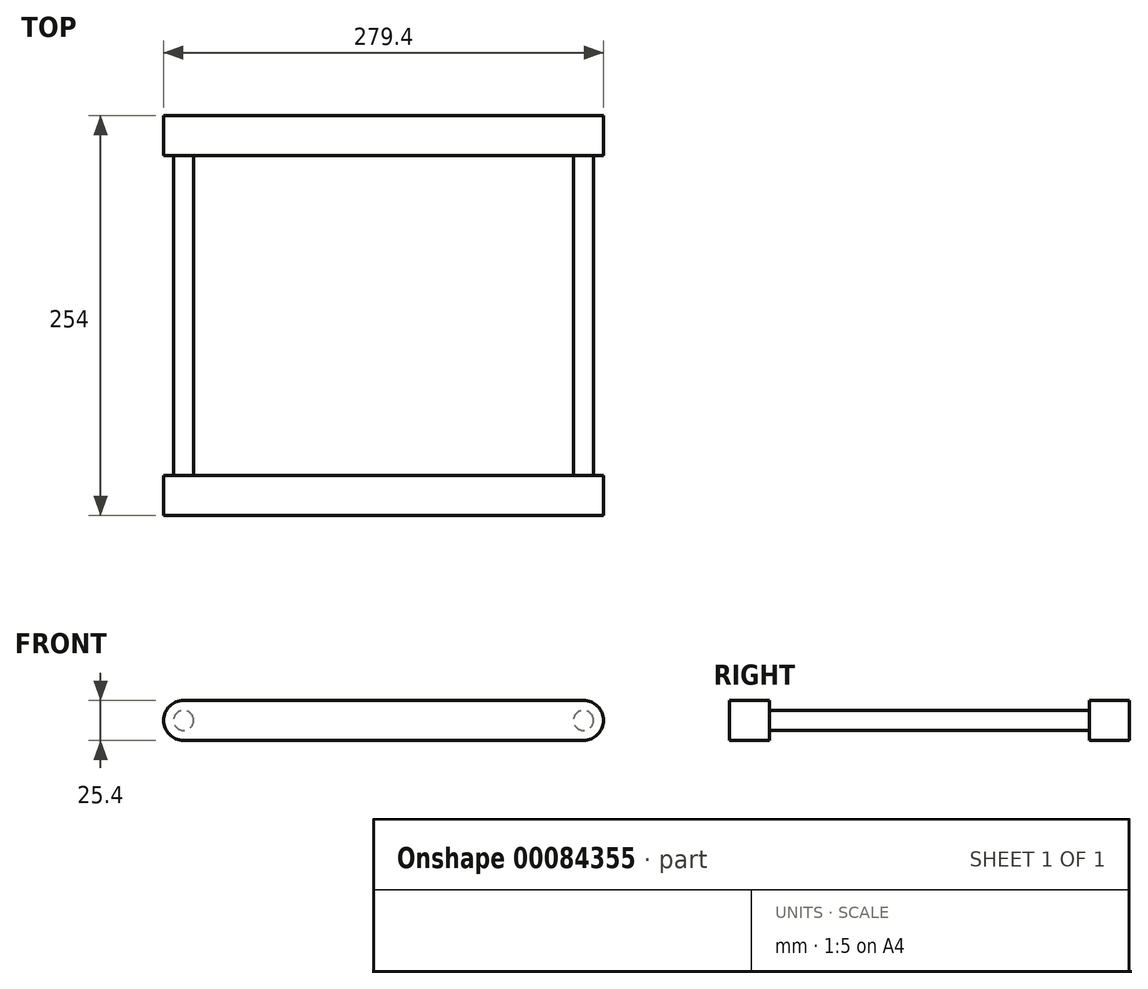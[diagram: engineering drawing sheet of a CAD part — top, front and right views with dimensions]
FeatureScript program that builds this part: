
annotation { "Feature Type Name" : "Feature", "Feature Type Description" : "" }
export const myFeature = defineFeature(function(context is Context, id is Id, definition is map)
    precondition{}
    {
        {
            var Q0;
            Q0=qCreatedBy(makeId("Front.planeOp"),FACE);
            var sketch = newSketch(context, id + "F0", { "sketchPlane" : qUnion([Q0])});
            skArc(sketch, "E0", {"start": v(0, -12.7) * mm, "mid": v(12.7, 0) * mm, "end": v(0, 12.7) * mm});
            skArc(sketch, "E1", {"start": v(-254, 12.7) * mm, "mid": v(-266.7, 0) * mm, "end": v(-254, -12.7) * mm});
            skLineSegment(sketch, "E2", {"start": v(-254, 12.7) * mm, "end": v(0, 12.7) * mm});
            skLineSegment(sketch, "E3", {"start": v(-254, -12.7) * mm, "end": v(0, -12.7) * mm});
            skLineSegment(sketch, "E4", {"start": v(0, 12.7) * mm, "end": v(-254, -12.7) * mm, "construction": true});
            skLineSegment(sketch, "E5", {"start": v(-254, 12.7) * mm, "end": v(0, -12.7) * mm, "construction": true});
            skSolve(sketch);
        }
        {
            var Q0;
            Q0=makeQuery(id+"F0.imprint","IMPRINT",FACE,{"disambiguationData":[TD([[makeQuery(id+"F0.imprint","IMPRINT",EDGE,{"derivedFrom":sQuery(id+"F0.wireOp",EDGE,"E0")}),1.0]])]});
            extrude(context, id + "F1", {"entities" : qUnion([Q0]), "depth" : 25.4 * mm});
        }
        {
            var Q0;
            Q0=makeQuery(id+"F1.opExtrude","CAP_FACE",FACE,{"disambiguationData":[OSD([sQuery(id+"F0.wireOp",EDGE,"E0"),sQuery(id+"F0.wireOp",EDGE,"E1"),sQuery(id+"F0.wireOp",EDGE,"E2"),sQuery(id+"F0.wireOp",EDGE,"E3")])],"isStart":false});
            var sketch = newSketch(context, id + "F2", { "sketchPlane" : qUnion([Q0])});
            skLineSegment(sketch, "E6.0", {"start": v(-254, 12.7) * mm, "end": v(0, 12.7) * mm});
            skArc(sketch, "E6.1", {"start": v(-254, 12.7) * mm, "mid": v(-266.7, 0) * mm, "end": v(-254, -12.7) * mm});
            skLineSegment(sketch, "E6.2", {"start": v(-254, -12.7) * mm, "end": v(0, -12.7) * mm});
            skArc(sketch, "E6.3", {"start": v(0, -12.7) * mm, "mid": v(12.7, 0) * mm, "end": v(0, 12.7) * mm});
            skCircle(sketch, "E7", {"center": v(-254, 0) * mm, "radius": 6.35 * mm});
            skCircle(sketch, "E8", {"center": v(0, 0) * mm, "radius": 6.35 * mm});
            skSolve(sketch);
        }
        {
            var Q0;
            Q0=makeQuery(id+"F2.imprint","IMPRINT",FACE,{"disambiguationData":[TD([[makeQuery(id+"F2.imprint","IMPRINT",EDGE,{"derivedFrom":sQuery(id+"F2.wireOp",EDGE,"E7")}),1.0]])]});
            var Q1;
            Q1=makeQuery(id+"F2.imprint","IMPRINT",FACE,{"disambiguationData":[TD([[makeQuery(id+"F2.imprint","IMPRINT",EDGE,{"derivedFrom":sQuery(id+"F2.wireOp",EDGE,"E8")}),1.0]])]});
            extrude(context, id + "F3", {"entities" : qUnion([Q0, Q1]), "operationType" : NewBodyOperationType.ADD, "depth" : 203.2 * mm});
        }
        {
            var Q0;
            Q0=makeQuery(id+"F3.opExtrude","CAP_FACE",FACE,{"disambiguationData":[OSD([sQuery(id+"F2.wireOp",EDGE,"E7")])],"isStart":false});
            var sketch = newSketch(context, id + "F4", { "sketchPlane" : qUnion([Q0])});
            skLineSegment(sketch, "E9.0", {"start": v(-254, 12.7) * mm, "end": v(0, 12.7) * mm});
            skArc(sketch, "E9.1", {"start": v(-254, 12.7) * mm, "mid": v(-266.7, 0) * mm, "end": v(-254, -12.7) * mm});
            skLineSegment(sketch, "E9.2", {"start": v(-254, -12.7) * mm, "end": v(0, -12.7) * mm});
            skArc(sketch, "E9.3", {"start": v(0, -12.7) * mm, "mid": v(12.7, 0) * mm, "end": v(0, 12.7) * mm});
            skSolve(sketch);
        }
        {
            var Q0;
            Q0=makeQuery(id+"F4.imprint","IMPRINT",FACE,{"disambiguationData":[TD([[makeQuery(id+"F4.imprint","IMPRINT",EDGE,{"derivedFrom":sQuery(id+"F4.wireOp",EDGE,"E9.0")}),-1.0]])]});
            var Q1;
            Q1=makeQuery(id+"F4.imprint","IMPRINT",FACE,{"disambiguationData":[TD([[makeQuery(id+"F4.imprint","IMPRINT",EDGE,{"derivedFrom":makeQuery(id+"F3.opExtrude","CAP_EDGE",EDGE,{"disambiguationData":[OSD([sQuery(id+"F2.wireOp",EDGE,"E7")])],"isStart":false})}),1.0]])]});
            extrude(context, id + "F5", {"entities" : qUnion([Q0, Q1]), "operationType" : NewBodyOperationType.ADD, "depth" : 25.4 * mm});
        }
    });
